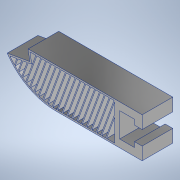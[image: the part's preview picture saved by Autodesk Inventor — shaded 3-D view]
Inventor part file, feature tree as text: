
AUTODESK INVENTOR PART (.ipt)
format: ipt  version: 2022 (Build 260153000, 153)  size: 366,080 bytes
history: native  units: mm
features: extrude x5, sketch x3, fillet x1, shell x1, projected_geometry x1
ambient origin geometry x8: Origin, YZ Plane, XZ Plane, XY Plane, X Axis, Y Axis, Z Axis, Center Point
bodies: Body1 (feature_tree)
feature tree (11):
  extrude  "Extrusion2"  Depth=5.8mm
  extrude  "Extrusion5"  Depth=12.0mm TaperAngle=0.0deg
  fillet  "Fillet2"  Radius=45.0mm
  shell  "Shell1"  Thickness=15.6mm
  extrude  "Extrusion7"  TaperAngle=0.0deg  [1 undecoded]
  extrude  "Extrusion8"  Depth=5.6mm
  extrude  "Extrusion9"  Depth=9.6mm
  sketch  "Sketch8"  dims[d41=5.8mm d48=44.0mm]
  sketch  "Sketch13"  dims[d50=3.0mm d56=12.0mm d57=0.0mm d63=45.0mm d67=15.6mm d71=0.0mm]
  sketch  "Sketch14"  dims[d80=17.453293mm d82=0.0mm d83=0.0mm d87=5.6mm d88=9.6mm d95=4.0mm d96=9.0mm d97=15.6mm d98=23.0mm d99=0.62mm d100=12.0mm d101=0.0mm d102=10.747401mm d103=12.0mm d104=0.0mm d105=0.38mm d1=0.38mm d127=12.0mm d128=0.0mm d130=19.198622mm d132=19.198622mm d133=0.38mm d135=0.38mm d136=0.38mm d137=0.38mm d138=0.38mm d139=0.38mm d140=0.38mm d141=0.38mm d142=3.81mm d143=0.38mm d144=3.81mm d145=3.81mm d146=3.81mm d147=3.81mm d152=19.198622mm d153=0.38mm d154=0.38mm d155=0.38mm d156=0.38mm d157=0.38mm d158=0.38mm d159=0.38mm d160=0.38mm d161=0.38mm d162=0.38mm d163=1.905mm d164=1.905mm d165=1.905mm d166=1.905mm d167=1.905mm d168=1.905mm d169=1.905mm d170=1.905mm d171=3.919533mm d172=3.81mm d173=3.81mm d175=1.905mm d180=0.38mm d182=1.905mm d183=1.905mm d184=1.905mm]
  projected_geometry  "Projected Loop1"
note: 1 required parameter value undecoded (feature->parameter linkage not recoverable at this tier; creation-order binding heuristic only, values carry confidence <= 0.55)
